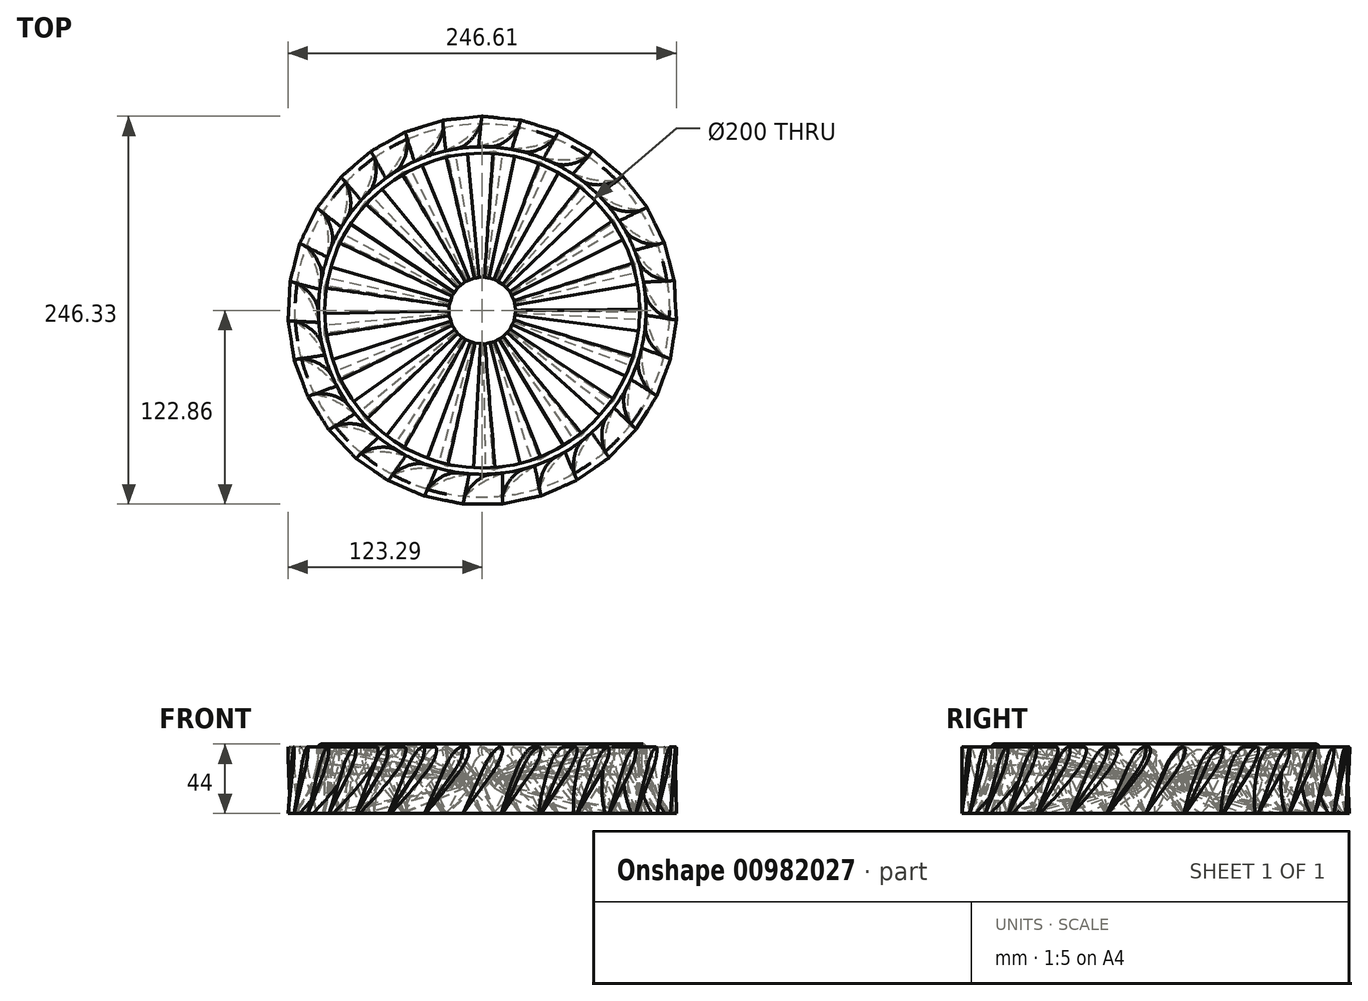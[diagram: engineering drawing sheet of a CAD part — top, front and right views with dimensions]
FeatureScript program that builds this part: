
annotation { "Feature Type Name" : "Feature", "Feature Type Description" : "" }
export const myFeature = defineFeature(function(context is Context, id is Id, definition is map)
    precondition{}
    {
        {
            var Q0;
            Q0=qCreatedBy(makeId("Right.planeOp"),FACE);
            cPlane(context, id + "F0", {"entities" : qUnion([Q0]), "cplaneType" : CPlaneType.OFFSET, "offset" : 100 * mm, "oppositeDirection" : true, "width" : 150 * mm, "height" : 150 * mm});
        }
        {
            var Q0;
            Q0=qCreatedBy(id+"F0.planeOp",FACE);
            var sketch = newSketch(context, id + "F1", { "sketchPlane" : qUnion([Q0])});
            skLineSegment(sketch, "E0.bottom", {"start": v(15.7, 0) * mm, "end": v(-15.7, 0) * mm, "construction": true});
            skLineSegment(sketch, "E0.top", {"start": v(15.7, 50) * mm, "end": v(-15.7, 50) * mm, "construction": true});
            skLineSegment(sketch, "E0.left", {"start": v(15.7, 0) * mm, "end": v(15.7, 50) * mm, "construction": true});
            skLineSegment(sketch, "E0.right", {"start": v(-15.7, 0) * mm, "end": v(-15.7, 50) * mm, "construction": true});
            skPoint(sketch, "E1", {"position": v(0, 0) * mm});
            skPoint(sketch, "E2", {"position": v(-7.7, 31.07) * mm});
            skEllipse(sketch, "E3", {"center": v(-7.7, 31.07) * mm, "majorRadius": 11.52 * mm, "minorRadius": 5 * mm, "majorAxis": v(-0.6, 0.8)});
            skLineSegment(sketch, "E4", {"start": v(-1.84, 31.22) * mm, "end": v(15.7, 0) * mm});
            skLineSegment(sketch, "E5", {"start": v(15.7, 0) * mm, "end": v(-9.47, 25.48) * mm});
            skPoint(sketch, "E6", {"position": v(-3.71, 34.08) * mm});
            skPoint(sketch, "E7", {"position": v(-11.7, 28.06) * mm});
            skLineSegment(sketch, "E8", {"start": v(-3.71, 34.08) * mm, "end": v(-7.7, 31.07) * mm, "construction": true});
            skLineSegment(sketch, "E9", {"start": v(-11.7, 28.06) * mm, "end": v(-7.7, 31.07) * mm, "construction": true});
            skLineSegment(sketch, "E10", {"start": v(-1.84, 31.22) * mm, "end": v(-9.47, 25.48) * mm, "construction": true});
            skLineSegment(sketch, "E11", {"start": v(-7.7, 31.07) * mm, "end": v(15.7, 0) * mm, "construction": true});
            skLineSegment(sketch, "E12.bottom", {"start": v(51.34, 60) * mm, "end": v(-48.66, 60) * mm});
            skLineSegment(sketch, "E12.top", {"start": v(51.34, 0) * mm, "end": v(-48.66, 0) * mm});
            skLineSegment(sketch, "E12.right", {"start": v(-48.66, 60) * mm, "end": v(-48.66, 0) * mm});
            skPoint(sketch, "E13", {"position": v(-13.05, 40.75) * mm});
            skLineSegment(sketch, "E14", {"start": v(-13.05, 40.75) * mm, "end": v(-23.99, 40.75) * mm, "construction": true});
            skLineSegment(sketch, "E15", {"start": v(-48.66, 40.75) * mm, "end": v(-48.66, 0) * mm, "construction": true});
            skPoint(sketch, "E16", {"position": v(0, 20.38) * mm});
            skPoint(sketch, "E16.positionSnap0", {"position": v(-48.66, 20.38) * mm});
            skSolve(sketch);
        }
        {
            var Q0;
            Q0=qCreatedBy(makeId("Right.planeOp"),FACE);
            cPlane(context, id + "F2", {"entities" : qUnion([Q0]), "cplaneType" : CPlaneType.OFFSET, "offset" : 21 * mm, "oppositeDirection" : true, "width" : 150 * mm, "height" : 150 * mm});
        }
        {
            var Q0;
            Q0=qCreatedBy(id+"F2.planeOp",FACE);
            var sketch = newSketch(context, id + "F3", { "sketchPlane" : qUnion([Q0])});
            skLineSegment(sketch, "E17.bottom", {"start": v(3.34, 16.04) * mm, "end": v(-3.34, 16.04) * mm, "construction": true});
            skLineSegment(sketch, "E17.top", {"start": v(3.34, 66.04) * mm, "end": v(-3.34, 66.04) * mm, "construction": true});
            skLineSegment(sketch, "E17.left", {"start": v(3.34, 16.04) * mm, "end": v(3.34, 66.04) * mm, "construction": true});
            skLineSegment(sketch, "E17.right", {"start": v(-3.34, 16.04) * mm, "end": v(-3.34, 66.04) * mm, "construction": true});
            skPoint(sketch, "E18", {"position": v(0, 16.04) * mm});
            skPoint(sketch, "E19", {"position": v(-1.64, 22.65) * mm});
            skEllipse(sketch, "E20", {"center": v(-1.64, 22.65) * mm, "majorRadius": 2.45 * mm, "minorRadius": 1.06 * mm, "majorAxis": v(-0.6, 0.8)});
            skLineSegment(sketch, "E21", {"start": v(-0.4, 22.68) * mm, "end": v(3.34, 16.04) * mm});
            skLineSegment(sketch, "E22", {"start": v(3.34, 16.04) * mm, "end": v(-2.01, 21.46) * mm});
            skPoint(sketch, "E23", {"position": v(-0.79, 23.3) * mm});
            skPoint(sketch, "E24", {"position": v(-2.49, 22.01) * mm});
            skLineSegment(sketch, "E25", {"start": v(-0.79, 23.3) * mm, "end": v(-1.64, 22.65) * mm, "construction": true});
            skLineSegment(sketch, "E26", {"start": v(-2.49, 22.01) * mm, "end": v(-1.64, 22.65) * mm, "construction": true});
            skLineSegment(sketch, "E27", {"start": v(-0.4, 22.68) * mm, "end": v(-2.01, 21.46) * mm, "construction": true});
            skLineSegment(sketch, "E28", {"start": v(-1.64, 22.65) * mm, "end": v(3.34, 16.04) * mm, "construction": true});
            skLineSegment(sketch, "E29.right", {"start": v(-42.27, -20.65) * mm, "end": v(-42.27, -80.65) * mm});
            skPoint(sketch, "E30", {"position": v(-2.78, 24.7) * mm});
            skLineSegment(sketch, "E31", {"start": v(-2.78, 24.7) * mm, "end": v(-17.6, 24.7) * mm, "construction": true});
            skLineSegment(sketch, "E32", {"start": v(-42.27, 24.7) * mm, "end": v(-42.27, -80.65) * mm, "construction": true});
            skPoint(sketch, "E33", {"position": v(6.4, -27.97) * mm});
            skPoint(sketch, "E33.positionSnap0", {"position": v(-42.27, -27.97) * mm});
            skLineSegment(sketch, "E34", {"start": v(-14.15, 16.04) * mm, "end": v(-14.15, 24.7) * mm, "construction": true});
            skPoint(sketch, "E35", {"position": v(0, 20.38) * mm});
            skPoint(sketch, "E35.positionSnap0", {"position": v(-14.15, 20.38) * mm});
            skSolve(sketch);
        }
        {
            var Q0;
            Q0=qSketchRegion(id+"F3",true);
            var Q1;
            Q1=qSketchRegion(id+"F1",true);
            loft(context, id + "F4", {"sheetProfilesArray" : [{ "sheetProfileEntities" : qUnion([Q0]) }, { "sheetProfileEntities" : qUnion([Q1]) }]});
        }
        {
            var Q0;
            Q0=qCreatedBy(makeId("Right.planeOp"),FACE);
            var sketch = newSketch(context, id + "F5", { "sketchPlane" : qUnion([Q0])});
            skLineSegment(sketch, "E36", {"start": v(0, 0) * mm, "end": v(0, 11.65) * mm, "construction": true});
            skPoint(sketch, "E37", {"position": v(-100, 0) * mm});
            skPoint(sketch, "E38", {"position": v(-100, 42) * mm});
            skLineSegment(sketch, "E39", {"start": v(-100, 42) * mm, "end": v(-100, 31.5) * mm});
            skPoint(sketch, "E40", {"position": v(-102, 42) * mm});
            skArc(sketch, "E41", {"start": v(-100, 42) * mm, "mid": v(-102, 44) * mm, "end": v(-104, 42) * mm});
            skArc(sketch, "E42", {"start": v(-118.59, 1.64) * mm, "mid": v(-107.76, 20.54) * mm, "end": v(-104, 42) * mm});
            skLineSegment(sketch, "E43", {"start": v(-117.82, 0) * mm, "end": v(-115.46, 0) * mm});
            skPoint(sketch, "E44.visualSharp", {"position": v(-120, 0) * mm});
            skArc(sketch, "E44.filletArc", {"start": v(-118.59, 1.64) * mm, "mid": v(-118.73, 0.58) * mm, "end": v(-117.82, 0) * mm});
            skArc(sketch, "E45", {"start": v(-111.8, 1.59) * mm, "mid": v(-103.06, 15.42) * mm, "end": v(-100, 31.5) * mm});
            skPoint(sketch, "E46.orphan", {"position": v(-100, 21) * mm});
            skPoint(sketch, "E47.orphan", {"position": v(-108.9, 0) * mm});
            skPoint(sketch, "E48.visualSharp", {"position": v(-113.36, 0) * mm});
            skArc(sketch, "E48.filletArc", {"start": v(-115.46, 0) * mm, "mid": v(-113.47, 0.41) * mm, "end": v(-111.8, 1.59) * mm});
            skPoint(sketch, "E49", {"position": v(-118.82, 1.08) * mm});
            skSolve(sketch);
        }
        {
            var Q0;
            {var subQ0=sQuery(id+"F3.wireOp",EDGE,"E20");var subQ1=makeQuery(id+"F3.imprint","INTERSECT",VERTEX,{"derivedFrom":[subQ0,sQuery(id+"F3.wireOp",EDGE,"E21")]});var subQ3=sQuery(id+"F1.wireOp",EDGE,"E3");var subQ4=makeQuery(id+"F1.imprint","INTERSECT",VERTEX,{"derivedFrom":[subQ3,sQuery(id+"F1.wireOp",EDGE,"E4")]});Q0=makeQuery(id+"F4.opLoft","SWEPT_BODY",BODY,{"disambiguationData":[OSD([makeQuery(id+"F1.imprint","IMPRINT",FACE,{"disambiguationData":[TD([[makeQuery(id+"F1.imprint","IMPRINT",EDGE,{"disambiguationData":[TD([[subQ4,1.0]])],"derivedFrom":subQ3}),1.0]])]}),makeQuery(id+"F3.imprint","IMPRINT",FACE,{"disambiguationData":[TD([[makeQuery(id+"F3.imprint","IMPRINT",EDGE,{"disambiguationData":[TD([[subQ1,1.0]])],"derivedFrom":subQ0}),1.0]])]})])]});}
            var Q1;
            Q1=sQuery(id+"F5.wireOp",EDGE,"E36");
            circularPattern(context, id + "F6", {"entities" : qUnion([Q0]), "axis" : qUnion([Q1]), "angle" : 360 * degree, "instanceCount" : 21, "equalSpace" : true});
        }
        {
            var Q0;
            Q0=makeQuery(id+"F5.imprint","IMPRINT",FACE,{"disambiguationData":[TD([[makeQuery(id+"F5.imprint","IMPRINT",EDGE,{"derivedFrom":sQuery(id+"F5.wireOp",EDGE,"E39")}),-1.0]])]});
            var Q1;
            Q1=sQuery(id+"F5.wireOp",EDGE,"E36");
            revolve(context, id + "F7", {"surfaceOperationType" : NewSurfaceOperationType.NEW, "entities" : qUnion([Q0]), "axis" : qUnion([Q1]), "revolveType" : RevolveType.FULL, "oppositeDirection" : true});
        }
        {
            var Q0;
            Q0=qCreatedBy(makeId("Front.planeOp"),FACE);
            cPlane(context, id + "F8", {"entities" : qUnion([Q0]), "cplaneType" : CPlaneType.OFFSET, "offset" : 122.8 * mm, "width" : 150 * mm, "height" : 150 * mm});
        }
        {
            var Q0;
            Q0=qCreatedBy(id+"F8.planeOp",FACE);
            var sketch = newSketch(context, id + "F9", { "sketchPlane" : qUnion([Q0])});
            skPoint(sketch, "E50", {"position": v(0, 42) * mm});
            skPoint(sketch, "E51", {"position": v(12.12, 42) * mm});
            skPoint(sketch, "E52", {"position": v(-12.12, 0) * mm});
            skLineSegment(sketch, "E53", {"start": v(12.12, 42) * mm, "end": v(-12.12, 0) * mm, "construction": true});
            skLineSegment(sketch, "E54", {"start": v(0, 0) * mm, "end": v(35.61, 0) * mm, "construction": true});
            skPoint(sketch, "E55", {"position": v(0, 21) * mm});
            skLineSegment(sketch, "E56", {"start": v(0, 21) * mm, "end": v(12.12, 42) * mm, "construction": true});
            skPoint(sketch, "E57", {"position": v(6.06, 31.5) * mm});
            skEllipse(sketch, "E58", {"center": v(6.06, 31.5) * mm, "majorRadius": 12.12 * mm, "minorRadius": 3.4 * mm, "majorAxis": v(0.5, 0.87)});
            skLineSegment(sketch, "E59", {"start": v(-12.12, 0) * mm, "end": v(1.27, 29.6) * mm});
            skLineSegment(sketch, "E60", {"start": v(-12.12, 0) * mm, "end": v(6.82, 26.4) * mm});
            skPoint(sketch, "E61", {"position": v(3.12, 33.2) * mm});
            skPoint(sketch, "E62", {"position": v(9, 29.8) * mm});
            skLineSegment(sketch, "E63", {"start": v(3.12, 33.2) * mm, "end": v(9, 29.8) * mm, "construction": true});
            skLineSegment(sketch, "E64", {"start": v(1.27, 29.6) * mm, "end": v(6.82, 26.4) * mm, "construction": true});
            skSolve(sketch);
        }
        {
            var Q0;
            Q0=qSketchRegion(id+"F9",true);
            var Q1;
            Q1=makeQuery(id+"F7.opRevolve","SWEPT_FACE",FACE,{"disambiguationData":[OSD([sQuery(id+"F5.wireOp",EDGE,"E42")])]});
            var Q2;
            Q2=makeQuery(id+"F7.opRevolve","SWEPT_BODY",BODY,{"disambiguationData":[OSD([sQuery(id+"F5.wireOp",EDGE,"E39"),sQuery(id+"F5.wireOp",EDGE,"E41"),sQuery(id+"F5.wireOp",EDGE,"E42"),sQuery(id+"F5.wireOp",EDGE,"E43"),sQuery(id+"F5.wireOp",EDGE,"E44.filletArc"),sQuery(id+"F5.wireOp",EDGE,"E45"),sQuery(id+"F5.wireOp",EDGE,"E48.filletArc")])]});
            extrude(context, id + "F10", {"entities" : qUnion([Q0]), "endBound" : BoundingType.UP_TO_BODY, "oppositeDirection" : true, "depth" : 25 * mm, "endBoundEntityFace" : qUnion([Q1]), "endBoundEntityBody" : qUnion([Q2]), "offsetDistance" : 25 * mm});
        }
        {
            var Q0;
            Q0=makeQuery(id+"F10.opExtrude","SWEPT_BODY",BODY,{"disambiguationData":[OSD([sQuery(id+"F9.wireOp",EDGE,"E58"),sQuery(id+"F9.wireOp",EDGE,"E59"),sQuery(id+"F9.wireOp",EDGE,"E60")])]});
            var Q1;
            Q1=sQuery(id+"F5.wireOp",EDGE,"E36");
            circularPattern(context, id + "F11", {"entities" : qUnion([Q0]), "axis" : qUnion([Q1]), "angle" : 360 * degree, "instanceCount" : 31, "equalSpace" : true});
        }
    });
